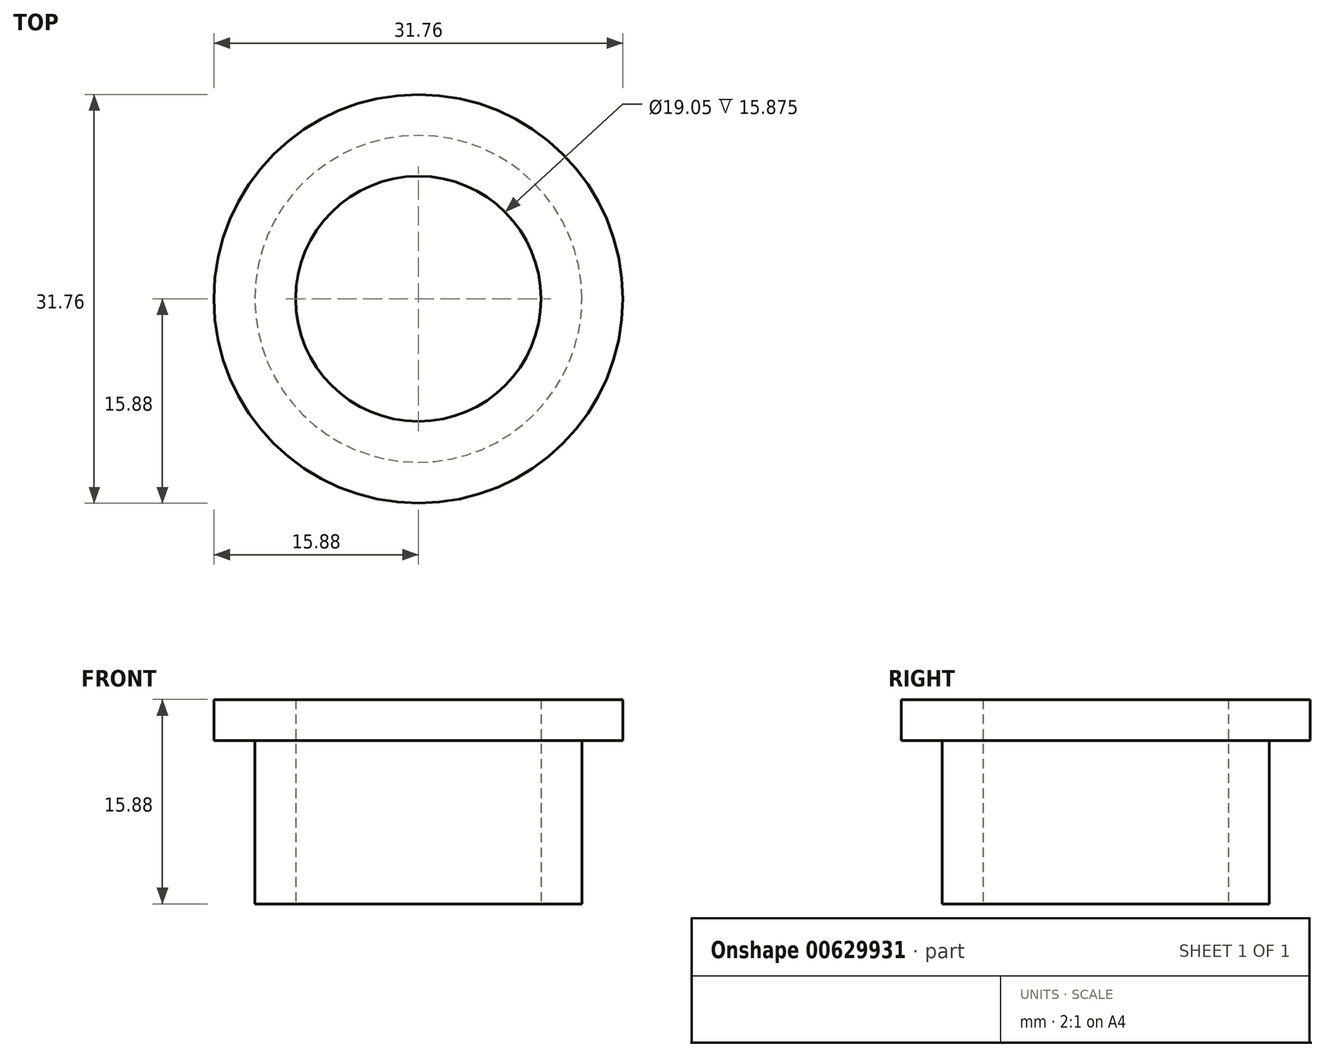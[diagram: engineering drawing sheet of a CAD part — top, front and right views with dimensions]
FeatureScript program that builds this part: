
annotation { "Feature Type Name" : "Feature", "Feature Type Description" : "" }
export const myFeature = defineFeature(function(context is Context, id is Id, definition is map)
    precondition{}
    {
        {
            var Q0;
            Q0=qCreatedBy(makeId("Front.planeOp"),FACE);
            var sketch = newSketch(context, id + "F0", { "sketchPlane" : qUnion([Q0])});
            skLineSegment(sketch, "E0", {"start": v(0, 0) * mm, "end": v(0, 25.4) * mm, "construction": true});
            skLineSegment(sketch, "E1.bottom", {"start": v(9.52, 0) * mm, "end": v(12.7, 0) * mm});
            skLineSegment(sketch, "E1.top", {"start": v(9.52, 12.7) * mm, "end": v(12.7, 12.7) * mm});
            skLineSegment(sketch, "E1.left", {"start": v(9.53, 0) * mm, "end": v(9.52, 12.7) * mm});
            skLineSegment(sketch, "E1.right", {"start": v(12.7, 0) * mm, "end": v(12.7, 12.7) * mm});
            skLineSegment(sketch, "E2.bottom", {"start": v(9.52, 12.7) * mm, "end": v(15.88, 12.7) * mm});
            skLineSegment(sketch, "E2.top", {"start": v(9.52, 15.88) * mm, "end": v(15.88, 15.88) * mm});
            skLineSegment(sketch, "E2.left", {"start": v(9.52, 12.7) * mm, "end": v(9.52, 15.88) * mm});
            skLineSegment(sketch, "E2.right", {"start": v(15.88, 12.7) * mm, "end": v(15.88, 15.88) * mm});
            skSolve(sketch);
        }
        {
            var Q0;
            Q0 = qSketchRegion(id + "F0", true);
            var Q1;
            Q1=sQuery(id+"F0.wireOp",EDGE,"E0");
            revolve(context, id + "F1", {"entities" : qUnion([Q0]), "axis" : qUnion([Q1]), "revolveType" : RevolveType.FULL});
        }
    });
